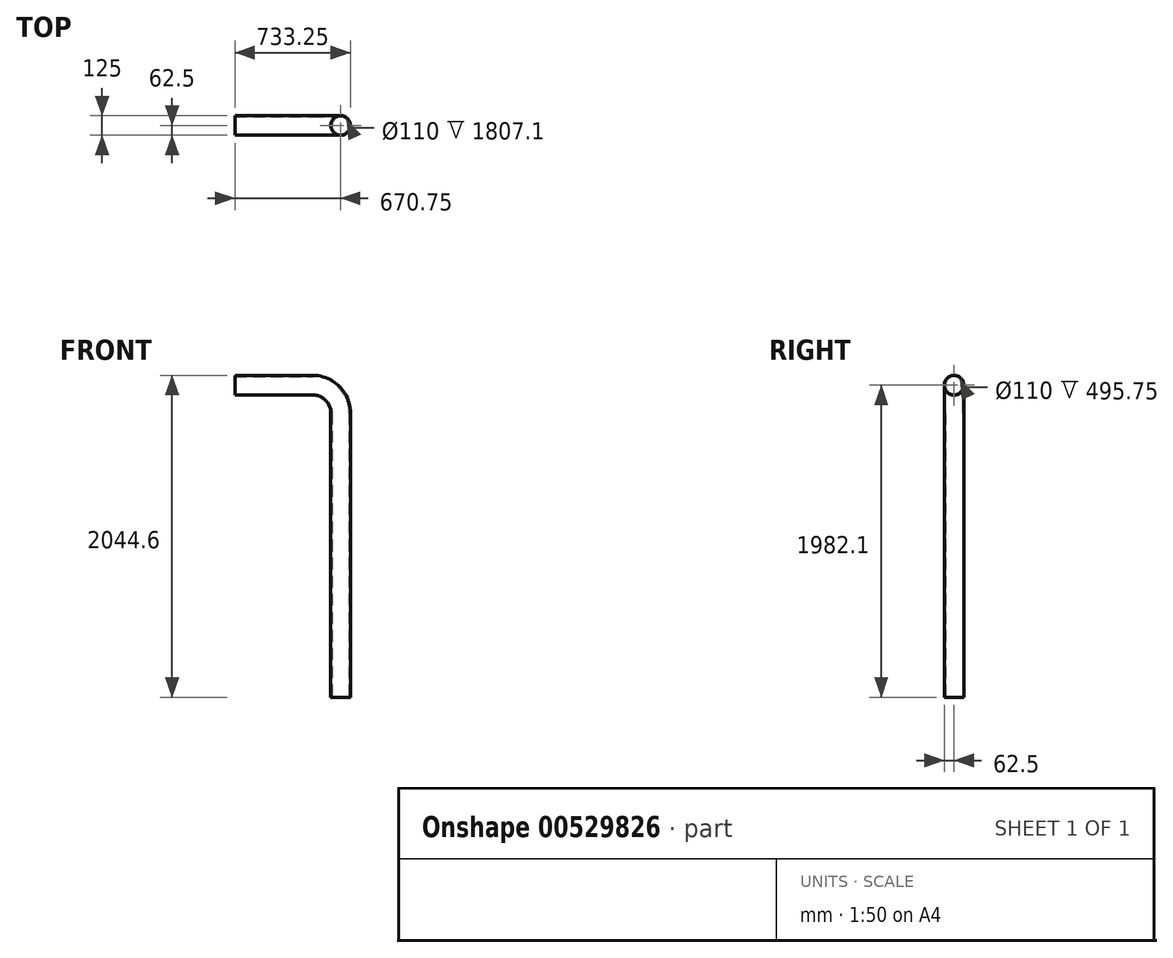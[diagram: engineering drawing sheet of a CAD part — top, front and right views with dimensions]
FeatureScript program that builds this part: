
annotation { "Feature Type Name" : "Feature", "Feature Type Description" : "" }
export const myFeature = defineFeature(function(context is Context, id is Id, definition is map)
    precondition{}
    {
        {
            var Q0;
            Q0=qCreatedBy(makeId("Front.planeOp"),FACE);
            var sketch = newSketch(context, id + "F0", { "sketchPlane" : qUnion([Q0])});
            skLineSegment(sketch, "E0", {"start": v(0, 0) * mm, "end": v(495.75, 0) * mm});
            skLineSegment(sketch, "E1", {"start": v(670.75, -175) * mm, "end": v(670.75, -1982.1) * mm});
            skPoint(sketch, "E2.visualSharp", {"position": v(670.75, 0) * mm});
            skArc(sketch, "E2.filletArc", {"start": v(670.75, -175) * mm, "mid": v(619.5, -51.26) * mm, "end": v(495.75, 0) * mm});
            skSolve(sketch);
        }
        {
            var Q0;
            Q0=qCreatedBy(makeId("Right.planeOp"),FACE);
            var sketch = newSketch(context, id + "F1", { "sketchPlane" : qUnion([Q0])});
            skCircle(sketch, "E3", {"center": v(0, 0) * mm, "radius": 62.5 * mm});
            skCircle(sketch, "E4", {"center": v(0, 0) * mm, "radius": 55 * mm});
            skSolve(sketch);
        }
        {
            var Q0;
            Q0=makeQuery(id+"F1.imprint","IMPRINT",FACE,{"disambiguationData":[TD([[makeQuery(id+"F1.imprint","IMPRINT",EDGE,{"derivedFrom":sQuery(id+"F1.wireOp",EDGE,"E3")}),1.0]])]});
            var Q1;
            Q1=sQuery(id+"F0.wireOp",EDGE,"E0");
            var Q2;
            Q2=sQuery(id+"F0.wireOp",EDGE,"c5145125-9687-4fce-a28a-6f7676226361.filletArc");
            var Q3;
            Q3=sQuery(id+"F0.wireOp",EDGE,"E2.filletArc");
            var Q4;
            Q4=sQuery(id+"F0.wireOp",EDGE,"E1");
            sweep(context, id + "F2", {"profiles" : qUnion([Q0]), "path" : qUnion([Q1, Q2, Q3, Q4])});
        }
    });
